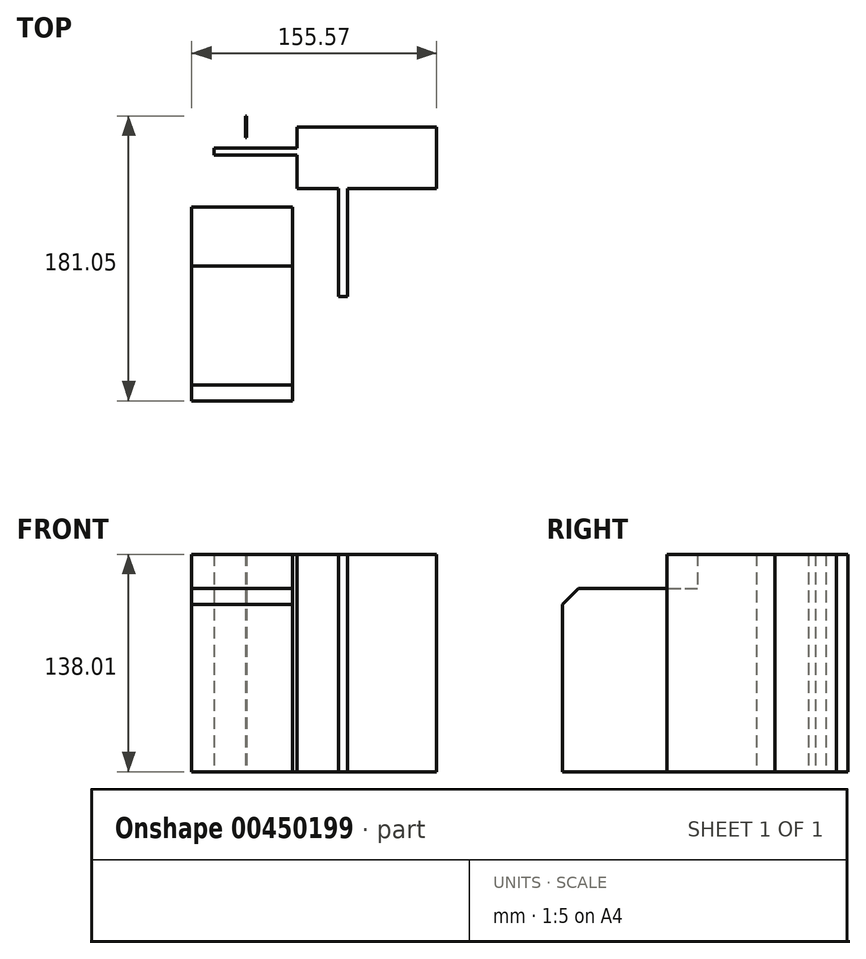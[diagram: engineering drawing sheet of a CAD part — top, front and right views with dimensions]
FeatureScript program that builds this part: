
annotation { "Feature Type Name" : "Feature", "Feature Type Description" : "" }
export const myFeature = defineFeature(function(context is Context, id is Id, definition is map)
    precondition{}
    {
        {
            var Q0;
            Q0=qCreatedBy(makeId("Top.planeOp"),FACE);
            var sketch = newSketch(context, id + "F0", { "sketchPlane" : qUnion([Q0])});
            skLineSegment(sketch, "E0.bottom", {"start": v(34.88, 33.27) * mm, "end": v(29.28, 33.27) * mm});
            skLineSegment(sketch, "E0.top", {"start": v(34.88, -68.81) * mm, "end": v(29.28, -68.81) * mm});
            skLineSegment(sketch, "E0.left", {"start": v(34.88, 33.27) * mm, "end": v(34.88, -68.81) * mm});
            skLineSegment(sketch, "E0.right", {"start": v(29.28, 33.27) * mm, "end": v(29.28, -68.81) * mm});
            skPoint(sketch, "E0.middle", {"position": v(32.08, -17.77) * mm});
            skLineSegment(sketch, "E1.bottom", {"start": v(-29.2, 32.37) * mm, "end": v(-29.86, 32.37) * mm});
            skLineSegment(sketch, "E1.top", {"start": v(-29.2, 46.07) * mm, "end": v(-29.86, 46.07) * mm});
            skLineSegment(sketch, "E1.left", {"start": v(-29.2, 32.37) * mm, "end": v(-29.2, 46.07) * mm});
            skLineSegment(sketch, "E1.right", {"start": v(-29.86, 32.37) * mm, "end": v(-29.86, 46.07) * mm});
            skPoint(sketch, "E1.middle", {"position": v(-29.53, 39.22) * mm});
            skLineSegment(sketch, "E2.bottom", {"start": v(-49.97, 21.14) * mm, "end": v(26.45, 21.14) * mm});
            skLineSegment(sketch, "E2.top", {"start": v(-49.97, 25.63) * mm, "end": v(26.45, 25.63) * mm});
            skLineSegment(sketch, "E2.left", {"start": v(-49.97, 21.14) * mm, "end": v(-49.97, 25.63) * mm});
            skLineSegment(sketch, "E2.right", {"start": v(26.45, 21.14) * mm, "end": v(26.45, 25.63) * mm});
            skPoint(sketch, "E2.middle", {"position": v(-11.76, 23.38) * mm});
            skLineSegment(sketch, "E3.bottom", {"start": v(0, -49.47) * mm, "end": v(-64.03, -49.47) * mm});
            skLineSegment(sketch, "E3.top", {"start": v(0, -12) * mm, "end": v(-64.03, -12) * mm});
            skLineSegment(sketch, "E3.left", {"start": v(0, -49.47) * mm, "end": v(0, -12) * mm});
            skLineSegment(sketch, "E3.right", {"start": v(-64.03, -49.47) * mm, "end": v(-64.03, -12) * mm});
            skPoint(sketch, "E3.middle", {"position": v(-32.02, -30.74) * mm});
            skLineSegment(sketch, "E4.bottom", {"start": v(91.54, 0) * mm, "end": v(2.97, 0) * mm});
            skLineSegment(sketch, "E4.top", {"start": v(91.54, 38.98) * mm, "end": v(2.97, 38.98) * mm});
            skLineSegment(sketch, "E4.left", {"start": v(91.54, 0) * mm, "end": v(91.54, 38.98) * mm});
            skLineSegment(sketch, "E4.right", {"start": v(2.97, 0) * mm, "end": v(2.97, 38.98) * mm});
            skPoint(sketch, "E4.middle", {"position": v(47.25, 19.5) * mm});
            skSolve(sketch);
        }
        {
            var Q0;
            Q0=makeQuery(id+"F0.imprint","IMPRINT",FACE,{"disambiguationData":[TD([[makeQuery(id+"F0.imprint","IMPRINT",EDGE,{"derivedFrom":sQuery(id+"F0.wireOp",EDGE,"E3.bottom")}),-1.0]])]});
            extrude(context, id + "F1", {"entities" : qUnion([Q0]), "depth" : 116.33 * mm});
        }
        {
            var Q0;
            Q0=makeQuery(id+"F1.opExtrude","SWEPT_FACE",FACE,{"disambiguationData":[OSD([sQuery(id+"F0.wireOp",EDGE,"E3.bottom")])]});
            extrude(context, id + "F2", {"entities" : qUnion([Q0]), "operationType" : NewBodyOperationType.ADD, "depth" : 85.5 * mm});
        }
        {
            var Q0;
            {var subQ0=sQuery(id+"F0.wireOp",EDGE,"E3.bottom");Q0=makeQuery(id+"F2.opExtrude","CAP_EDGE",EDGE,{"disambiguationData":[OSD([subQ0]),TDD([makeQuery(id+"F1.opExtrude","CAP_EDGE",EDGE,{"disambiguationData":[OSD([subQ0])],"isStart":false})])],"isStart":false});}
            chamfer(context, id + "F3", {"entities" : qUnion([Q0]), "width" : 10 * mm, "tangentPropagation" : true});
        }
        {
            var Q0;
            Q0 = qSketchRegion(id + "F0", true);
            var Q1;
            {var subQ1=sQuery(id+"F0.wireOp",EDGE,"E0.bottom");Q1=makeQuery(id+"F0.imprint","IMPRINT",FACE,{"disambiguationData":[TD([[makeQuery(id+"F0.imprint","IMPRINT",EDGE,{"derivedFrom":subQ1}),-1.0]])]});}
            extrude(context, id + "F4", {"entities" : qUnion([Q0, Q1]), "operationType" : NewBodyOperationType.ADD, "depth" : 138 * mm});
        }
    });
